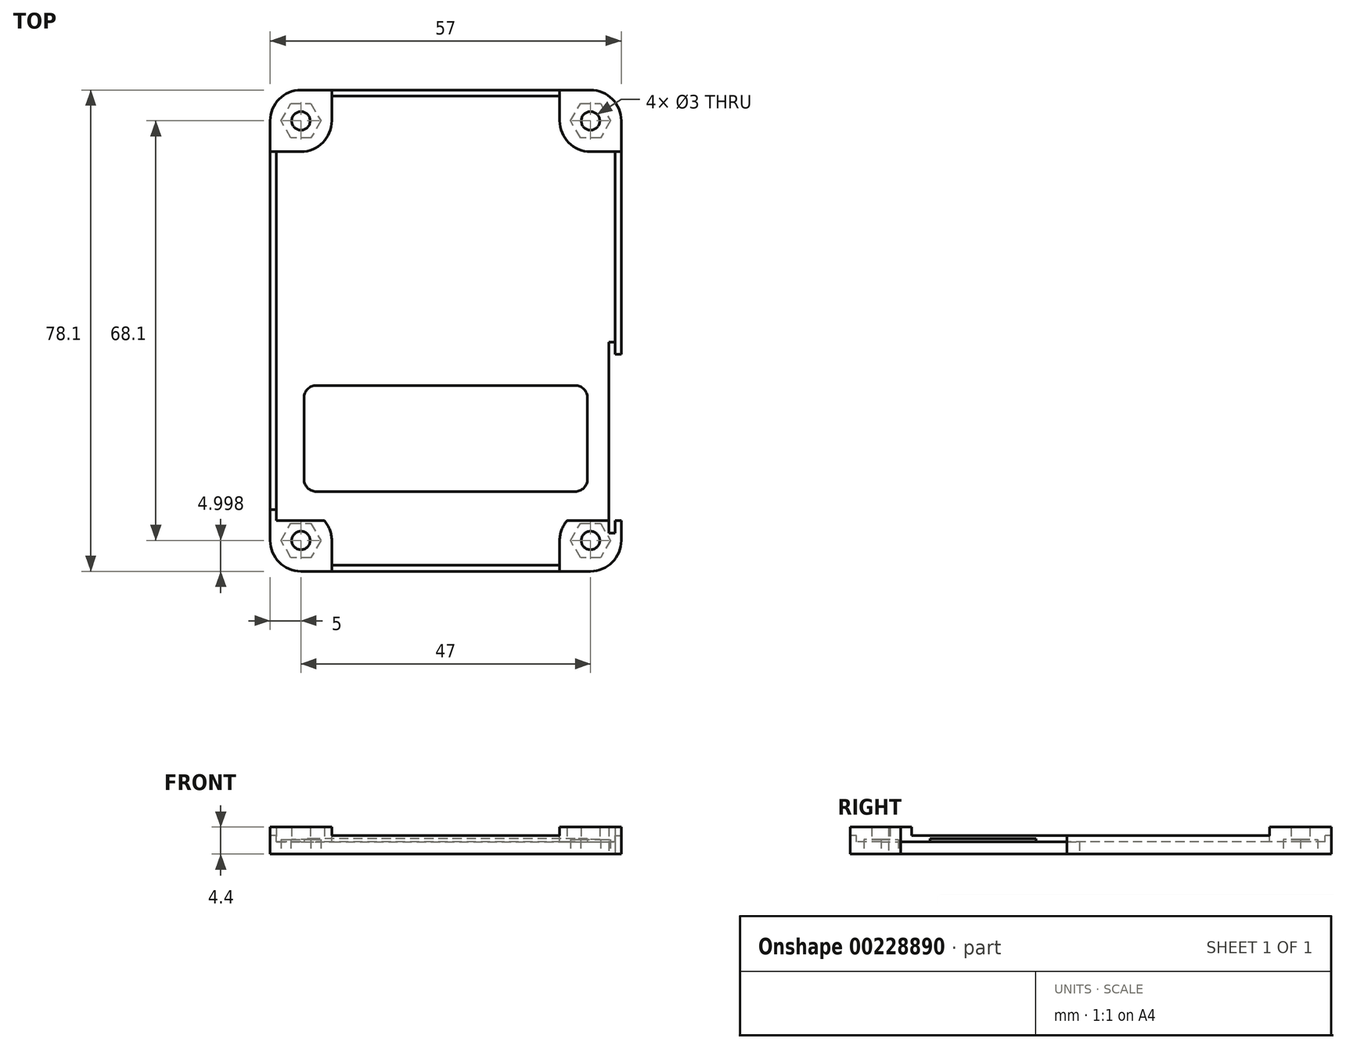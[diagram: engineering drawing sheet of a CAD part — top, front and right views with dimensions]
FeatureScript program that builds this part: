
annotation { "Feature Type Name" : "Feature", "Feature Type Description" : "" }
export const myFeature = defineFeature(function(context is Context, id is Id, definition is map)
    precondition{}
    {
        {
            var Q0;
            Q0=qCreatedBy(makeId("Top.planeOp"),FACE);
            var sketch = newSketch(context, id + "F0", { "sketchPlane" : qUnion([Q0])});
            skLineSegment(sketch, "E0.bottom", {"start": v(-20.39, 18.87) * mm, "end": v(6.91, 18.87) * mm, "construction": true});
            skLineSegment(sketch, "E0.top", {"start": v(-20.39, -8.93) * mm, "end": v(6.91, -8.93) * mm, "construction": true});
            skLineSegment(sketch, "E0.left", {"start": v(-20.39, 18.87) * mm, "end": v(-20.39, -8.93) * mm, "construction": true});
            skLineSegment(sketch, "E0.right", {"start": v(6.91, 18.87) * mm, "end": v(6.91, -8.93) * mm, "construction": true});
            skLineSegment(sketch, "E1.bottom", {"start": v(-24.24, 20.8) * mm, "end": v(10.76, 20.8) * mm, "construction": true});
            skLineSegment(sketch, "E1.top", {"start": v(-24.24, -10.85) * mm, "end": v(10.76, -10.85) * mm, "construction": true});
            skLineSegment(sketch, "E1.left", {"start": v(-24.24, 20.8) * mm, "end": v(-24.24, -10.85) * mm, "construction": true});
            skLineSegment(sketch, "E1.right", {"start": v(10.76, 20.8) * mm, "end": v(10.76, -10.85) * mm, "construction": true});
            skLineSegment(sketch, "E2.bottom", {"start": v(-29.84, -16.15) * mm, "end": v(-29.84, -14.35) * mm, "construction": true});
            skLineSegment(sketch, "E2.top", {"start": v(3.26, -16.15) * mm, "end": v(3.26, -14.35) * mm, "construction": true});
            skLineSegment(sketch, "E2.left", {"start": v(-29.84, -16.15) * mm, "end": v(3.26, -16.15) * mm, "construction": true});
            skLineSegment(sketch, "E2.right", {"start": v(-25.74, -14.35) * mm, "end": v(3.26, -14.35) * mm, "construction": true});
            skLineSegment(sketch, "E3.bottom", {"start": v(-30.74, -14.35) * mm, "end": v(-30.74, -11.95) * mm, "construction": true});
            skLineSegment(sketch, "E3.top", {"start": v(-25.74, -14.35) * mm, "end": v(-25.74, -11.95) * mm, "construction": true});
            skLineSegment(sketch, "E3.left", {"start": v(-30.74, -14.35) * mm, "end": v(-29.84, -14.35) * mm, "construction": true});
            skLineSegment(sketch, "E3.right", {"start": v(-30.74, -11.95) * mm, "end": v(-25.74, -11.95) * mm, "construction": true});
            skLineSegment(sketch, "E4.bottom", {"start": v(-29.34, -20.15) * mm, "end": v(22.16, -20.15) * mm, "construction": true});
            skLineSegment(sketch, "E4.top", {"start": v(-29.34, -46.15) * mm, "end": v(22.16, -46.15) * mm, "construction": true});
            skLineSegment(sketch, "E4.left", {"start": v(-29.34, -20.15) * mm, "end": v(-29.34, -46.15) * mm, "construction": true});
            skLineSegment(sketch, "E4.right", {"start": v(22.16, -20.15) * mm, "end": v(22.16, -46.15) * mm, "construction": true});
            skLineSegment(sketch, "E5.bottom", {"start": v(-26.84, 23.3) * mm, "end": v(20.16, 23.3) * mm});
            skLineSegment(sketch, "E5.top", {"start": v(-26.84, -54.8) * mm, "end": v(20.16, -54.8) * mm});
            skLineSegment(sketch, "E5.left", {"start": v(-31.84, 18.3) * mm, "end": v(-31.84, -49.8) * mm});
            skLineSegment(sketch, "E5.right", {"start": v(25.16, 18.3) * mm, "end": v(25.16, -49.8) * mm});
            skArc(sketch, "E6.filletArc", {"start": v(-26.84, 23.3) * mm, "mid": v(-30.38, 21.83) * mm, "end": v(-31.84, 18.3) * mm});
            skArc(sketch, "E7.filletArc", {"start": v(20.16, -54.8) * mm, "mid": v(23.7, -53.34) * mm, "end": v(25.16, -49.8) * mm});
            skArc(sketch, "E8.filletArc", {"start": v(-31.84, -49.8) * mm, "mid": v(-30.38, -53.34) * mm, "end": v(-26.84, -54.8) * mm});
            skArc(sketch, "E9.filletArc", {"start": v(25.16, 18.3) * mm, "mid": v(23.7, 21.83) * mm, "end": v(20.16, 23.3) * mm});
            skCircle(sketch, "E10", {"center": v(-26.84, 18.3) * mm, "radius": 2.8 * mm, "construction": true});
            skCircle(sketch, "E11", {"center": v(20.16, 18.3) * mm, "radius": 2.8 * mm, "construction": true});
            skCircle(sketch, "E12", {"center": v(20.16, -49.8) * mm, "radius": 2.8 * mm, "construction": true});
            skCircle(sketch, "E13", {"center": v(-26.84, -49.8) * mm, "radius": 2.8 * mm, "construction": true});
            skLineSegment(sketch, "E14", {"start": v(17.96, 15.08) * mm, "end": v(17.96, -13) * mm, "construction": true});
            skLineSegment(sketch, "E15.0", {"start": v(18.54, 21.1) * mm, "end": v(21.78, 21.1) * mm});
            skLineSegment(sketch, "E15.1", {"start": v(21.78, 21.1) * mm, "end": v(23.4, 18.3) * mm});
            skLineSegment(sketch, "E15.2", {"start": v(23.4, 18.3) * mm, "end": v(21.78, 15.5) * mm});
            skLineSegment(sketch, "E15.3", {"start": v(21.78, 15.5) * mm, "end": v(18.54, 15.5) * mm});
            skLineSegment(sketch, "E15.4", {"start": v(18.54, 15.5) * mm, "end": v(16.93, 18.3) * mm});
            skLineSegment(sketch, "E15.5", {"start": v(16.93, 18.3) * mm, "end": v(18.54, 21.1) * mm});
            skPoint(sketch, "E15.0.midPoint", {"position": v(20.16, 21.1) * mm});
            skLineSegment(sketch, "E16.0", {"start": v(-28.46, 21.1) * mm, "end": v(-25.22, 21.1) * mm});
            skLineSegment(sketch, "E16.1", {"start": v(-25.22, 21.1) * mm, "end": v(-23.6, 18.3) * mm});
            skLineSegment(sketch, "E16.2", {"start": v(-23.6, 18.3) * mm, "end": v(-25.22, 15.5) * mm});
            skLineSegment(sketch, "E16.3", {"start": v(-25.22, 15.5) * mm, "end": v(-28.46, 15.5) * mm});
            skLineSegment(sketch, "E16.4", {"start": v(-28.46, 15.5) * mm, "end": v(-30.07, 18.3) * mm});
            skLineSegment(sketch, "E16.5", {"start": v(-30.07, 18.3) * mm, "end": v(-28.46, 21.1) * mm});
            skPoint(sketch, "E16.0.midPoint", {"position": v(-26.84, 21.1) * mm});
            skLineSegment(sketch, "E17.0", {"start": v(18.54, -47) * mm, "end": v(21.78, -47) * mm});
            skLineSegment(sketch, "E17.1", {"start": v(21.78, -47) * mm, "end": v(23.4, -49.8) * mm});
            skLineSegment(sketch, "E17.2", {"start": v(23.4, -49.8) * mm, "end": v(21.78, -52.6) * mm});
            skLineSegment(sketch, "E17.3", {"start": v(21.78, -52.6) * mm, "end": v(18.54, -52.6) * mm});
            skLineSegment(sketch, "E17.4", {"start": v(18.54, -52.6) * mm, "end": v(16.93, -49.8) * mm});
            skLineSegment(sketch, "E17.5", {"start": v(16.93, -49.8) * mm, "end": v(18.54, -47) * mm});
            skPoint(sketch, "E17.0.midPoint", {"position": v(20.16, -47) * mm});
            skLineSegment(sketch, "E18.0", {"start": v(-28.46, -47) * mm, "end": v(-25.22, -47) * mm});
            skLineSegment(sketch, "E18.1", {"start": v(-25.22, -47) * mm, "end": v(-23.6, -49.8) * mm});
            skLineSegment(sketch, "E18.2", {"start": v(-23.6, -49.8) * mm, "end": v(-25.22, -52.6) * mm});
            skLineSegment(sketch, "E18.3", {"start": v(-25.22, -52.6) * mm, "end": v(-28.46, -52.6) * mm});
            skLineSegment(sketch, "E18.4", {"start": v(-28.46, -52.6) * mm, "end": v(-30.07, -49.8) * mm});
            skLineSegment(sketch, "E18.5", {"start": v(-30.07, -49.8) * mm, "end": v(-28.46, -47) * mm});
            skPoint(sketch, "E18.0.midPoint", {"position": v(-26.84, -47) * mm});
            skSolve(sketch);
        }
        {
            var Q0;
            Q0 = qSketchRegion(id + "F0", true);
            extrude(context, id + "F1", {"entities" : qUnion([Q0]), "depth" : 2.4 * mm, "offsetDistance" : 25 * mm});
        }
        {
            var Q0;
            Q0=makeQuery(id+"F1.opExtrude","CAP_FACE",FACE,{"disambiguationData":[OSD([sQuery(id+"F0.wireOp",EDGE,"E5.bottom"),sQuery(id+"F0.wireOp",EDGE,"E5.top"),sQuery(id+"F0.wireOp",EDGE,"E5.left"),sQuery(id+"F0.wireOp",EDGE,"E5.right"),sQuery(id+"F0.wireOp",EDGE,"E6.filletArc"),sQuery(id+"F0.wireOp",EDGE,"E7.filletArc"),sQuery(id+"F0.wireOp",EDGE,"E8.filletArc"),sQuery(id+"F0.wireOp",EDGE,"E9.filletArc"),sQuery(id+"F0.wireOp",EDGE,"E15.0"),sQuery(id+"F0.wireOp",EDGE,"E15.1"),sQuery(id+"F0.wireOp",EDGE,"E15.2"),sQuery(id+"F0.wireOp",EDGE,"E15.3"),sQuery(id+"F0.wireOp",EDGE,"E15.4"),sQuery(id+"F0.wireOp",EDGE,"E15.5"),sQuery(id+"F0.wireOp",EDGE,"E16.0"),sQuery(id+"F0.wireOp",EDGE,"E16.1"),sQuery(id+"F0.wireOp",EDGE,"E16.2"),sQuery(id+"F0.wireOp",EDGE,"E16.3"),sQuery(id+"F0.wireOp",EDGE,"E16.4"),sQuery(id+"F0.wireOp",EDGE,"E16.5"),sQuery(id+"F0.wireOp",EDGE,"E17.0"),sQuery(id+"F0.wireOp",EDGE,"E17.1"),sQuery(id+"F0.wireOp",EDGE,"E17.2"),sQuery(id+"F0.wireOp",EDGE,"E17.3"),sQuery(id+"F0.wireOp",EDGE,"E17.4"),sQuery(id+"F0.wireOp",EDGE,"E17.5"),sQuery(id+"F0.wireOp",EDGE,"E18.0"),sQuery(id+"F0.wireOp",EDGE,"E18.1"),sQuery(id+"F0.wireOp",EDGE,"E18.2"),sQuery(id+"F0.wireOp",EDGE,"E18.3"),sQuery(id+"F0.wireOp",EDGE,"E18.4"),sQuery(id+"F0.wireOp",EDGE,"E18.5")])],"isStart":false});
            var sketch = newSketch(context, id + "F2", { "sketchPlane" : qUnion([Q0])});
            skArc(sketch, "E19", {"start": v(-26.84, 23.3) * mm, "mid": v(-30.38, 21.83) * mm, "end": v(-31.84, 18.3) * mm});
            skArc(sketch, "E20", {"start": v(25.16, 18.3) * mm, "mid": v(23.7, 21.83) * mm, "end": v(20.16, 23.3) * mm});
            skArc(sketch, "E21", {"start": v(16.33, -46.6) * mm, "mid": v(15.46, -48.1) * mm, "end": v(15.16, -49.8) * mm});
            skArc(sketch, "E22", {"start": v(-21.84, -49.8) * mm, "mid": v(-22.14, -48.1) * mm, "end": v(-23, -46.6) * mm});
            skCircle(sketch, "E23", {"center": v(-26.84, 18.3) * mm, "radius": 1.5 * mm});
            skCircle(sketch, "E24", {"center": v(20.16, 18.3) * mm, "radius": 1.5 * mm});
            skCircle(sketch, "E25", {"center": v(20.16, -49.8) * mm, "radius": 1.5 * mm});
            skCircle(sketch, "E26", {"center": v(-26.84, -49.8) * mm, "radius": 1.5 * mm});
            skLineSegment(sketch, "E27.bottom", {"start": v(-21.84, 23.3) * mm, "end": v(-26.84, 23.3) * mm});
            skLineSegment(sketch, "E27.top", {"start": v(-26.84, 13.3) * mm, "end": v(-31.84, 13.3) * mm});
            skLineSegment(sketch, "E27.left", {"start": v(-21.84, 23.3) * mm, "end": v(-21.84, 18.3) * mm});
            skLineSegment(sketch, "E27.right", {"start": v(-31.84, 18.3) * mm, "end": v(-31.84, 13.3) * mm});
            skLineSegment(sketch, "E28.bottom", {"start": v(15.16, 23.3) * mm, "end": v(20.16, 23.3) * mm});
            skLineSegment(sketch, "E28.top", {"start": v(20.16, 13.3) * mm, "end": v(25.16, 13.3) * mm});
            skLineSegment(sketch, "E28.left", {"start": v(15.16, 23.3) * mm, "end": v(15.16, 18.3) * mm});
            skLineSegment(sketch, "E28.right", {"start": v(25.16, 18.3) * mm, "end": v(25.16, 13.3) * mm});
            skLineSegment(sketch, "E29.bottom", {"start": v(25.16, -44.8) * mm, "end": v(24.16, -44.8) * mm});
            skLineSegment(sketch, "E29.top", {"start": v(20.16, -54.8) * mm, "end": v(15.16, -54.8) * mm});
            skLineSegment(sketch, "E29.left", {"start": v(25.16, -44.8) * mm, "end": v(25.16, -49.8) * mm});
            skLineSegment(sketch, "E29.right", {"start": v(15.16, -49.8) * mm, "end": v(15.16, -54.8) * mm});
            skLineSegment(sketch, "E30.bottom", {"start": v(-31.84, -44.8) * mm, "end": v(-30.84, -44.8) * mm});
            skLineSegment(sketch, "E30.top", {"start": v(-26.84, -54.8) * mm, "end": v(-21.84, -54.8) * mm});
            skLineSegment(sketch, "E30.left", {"start": v(-31.84, -44.8) * mm, "end": v(-31.84, -49.8) * mm});
            skLineSegment(sketch, "E30.right", {"start": v(-21.84, -49.8) * mm, "end": v(-21.84, -54.8) * mm});
            skArc(sketch, "E31.trimOffspring", {"start": v(-26.84, 13.3) * mm, "mid": v(-23.3, 14.76) * mm, "end": v(-21.84, 18.3) * mm});
            skArc(sketch, "E32.trimOffspring", {"start": v(15.16, 18.3) * mm, "mid": v(16.62, 14.76) * mm, "end": v(20.16, 13.3) * mm});
            skArc(sketch, "E33.trimOffspring", {"start": v(20.16, -54.8) * mm, "mid": v(23.7, -53.34) * mm, "end": v(25.16, -49.8) * mm});
            skArc(sketch, "E34.trimOffspring", {"start": v(-31.84, -49.8) * mm, "mid": v(-30.38, -53.34) * mm, "end": v(-26.84, -54.8) * mm});
            skLineSegment(sketch, "E35.bottom", {"start": v(-21.84, 23.3) * mm, "end": v(15.16, 23.3) * mm});
            skLineSegment(sketch, "E35.top", {"start": v(-21.84, 22.3) * mm, "end": v(15.16, 22.3) * mm});
            skLineSegment(sketch, "E35.left", {"start": v(-21.84, 23.3) * mm, "end": v(-21.84, 22.3) * mm});
            skLineSegment(sketch, "E35.right", {"start": v(15.16, 23.3) * mm, "end": v(15.16, 22.3) * mm});
            skLineSegment(sketch, "E36.bottom", {"start": v(-21.84, -54.8) * mm, "end": v(15.16, -54.8) * mm});
            skLineSegment(sketch, "E36.top", {"start": v(-21.84, -53.8) * mm, "end": v(15.16, -53.8) * mm});
            skLineSegment(sketch, "E36.left", {"start": v(-21.84, -54.8) * mm, "end": v(-21.84, -53.8) * mm});
            skLineSegment(sketch, "E36.right", {"start": v(15.16, -54.8) * mm, "end": v(15.16, -53.8) * mm});
            skLineSegment(sketch, "E37.bottom", {"start": v(25.16, 13.3) * mm, "end": v(24.16, 13.3) * mm});
            skLineSegment(sketch, "E37.left", {"start": v(25.16, 13.3) * mm, "end": v(25.16, -44.8) * mm});
            skLineSegment(sketch, "E37.right", {"start": v(24.16, 13.3) * mm, "end": v(24.16, -44.8) * mm});
            skLineSegment(sketch, "E38.bottom", {"start": v(-31.84, 13.3) * mm, "end": v(-30.84, 13.3) * mm});
            skLineSegment(sketch, "E38.left", {"start": v(-31.84, 13.3) * mm, "end": v(-31.84, -44.8) * mm});
            skLineSegment(sketch, "E38.right", {"start": v(-30.84, 13.3) * mm, "end": v(-30.84, -44.8) * mm});
            skLineSegment(sketch, "E39.top", {"start": v(-30.84, -46.6) * mm, "end": v(-23, -46.6) * mm});
            skLineSegment(sketch, "E39.left", {"start": v(-30.84, -43.24) * mm, "end": v(-30.84, -46.6) * mm});
            skLineSegment(sketch, "E39.right", {"start": v(24.16, -43.24) * mm, "end": v(24.16, -46.6) * mm});
            skLineSegment(sketch, "E40.trimOffspring", {"start": v(16.33, -46.6) * mm, "end": v(24.16, -46.6) * mm});
            skSolve(sketch);
        }
        {
            var Q0;
            Q0=makeQuery(id+"F2.imprint","IMPRINT",FACE,{"disambiguationData":[TD([[makeQuery(id+"F2.imprint","IMPRINT",EDGE,{"derivedFrom":sQuery(id+"F2.wireOp",EDGE,"E19")}),1.0]])]});
            var Q1;
            Q1=makeQuery(id+"F2.imprint","IMPRINT",FACE,{"disambiguationData":[TD([[makeQuery(id+"F2.imprint","IMPRINT",EDGE,{"derivedFrom":sQuery(id+"F2.wireOp",EDGE,"E20")}),1.0]])]});
            var Q2;
            {var subQ3=sQuery(id+"F2.wireOp",EDGE,"E21");Q2=makeQuery(id+"F2.imprint","IMPRINT",FACE,{"disambiguationData":[TD([[makeQuery(id+"F2.imprint","IMPRINT",EDGE,{"derivedFrom":subQ3}),1.0]])]});}
            var Q3;
            {var subQ3=sQuery(id+"F2.wireOp",EDGE,"E22");Q3=makeQuery(id+"F2.imprint","IMPRINT",FACE,{"disambiguationData":[TD([[makeQuery(id+"F2.imprint","IMPRINT",EDGE,{"derivedFrom":subQ3}),1.0]])]});}
            var Q4;
            Q4=makeQuery(id+"F2.imprint","IMPRINT",FACE,{"disambiguationData":[TD([[makeQuery(id+"F2.imprint","IMPRINT",EDGE,{"derivedFrom":sQuery(id+"F2.wireOp",EDGE,"E26")}),-1.0]])]});
            var Q5;
            Q5=makeQuery(id+"F2.imprint","IMPRINT",FACE,{"disambiguationData":[TD([[makeQuery(id+"F2.imprint","IMPRINT",EDGE,{"derivedFrom":sQuery(id+"F2.wireOp",EDGE,"E25")}),-1.0]])]});
            var Q6;
            Q6=makeQuery(id+"F2.imprint","IMPRINT",FACE,{"disambiguationData":[TD([[makeQuery(id+"F2.imprint","IMPRINT",EDGE,{"derivedFrom":sQuery(id+"F2.wireOp",EDGE,"E24")}),-1.0]])]});
            var Q7;
            Q7=makeQuery(id+"F2.imprint","IMPRINT",FACE,{"disambiguationData":[TD([[makeQuery(id+"F2.imprint","IMPRINT",EDGE,{"derivedFrom":sQuery(id+"F2.wireOp",EDGE,"E23")}),-1.0]])]});
            extrude(context, id + "F3", {"entities" : qUnion([Q0, Q1, Q2, Q3, Q4, Q5, Q6, Q7]), "operationType" : NewBodyOperationType.ADD, "depth" : 2 * mm, "offsetDistance" : 25 * mm});
        }
        {
            var Q0;
            {var subQ2=sQuery(id+"F2.wireOp",EDGE,"E21");Q0=makeQuery(id+"F2.imprint","IMPRINT",FACE,{"disambiguationData":[TD([[makeQuery(id+"F2.imprint","IMPRINT",EDGE,{"derivedFrom":subQ2}),-1.0]])]});}
            extrude(context, id + "F4", {"entities" : qUnion([Q0]), "operationType" : NewBodyOperationType.REMOVE, "oppositeDirection" : true, "depth" : 0.4 * mm, "offsetDistance" : 25 * mm});
        }
        {
            var Q0;
            {var subQ5=sQuery(id+"F2.wireOp",EDGE,"E30.bottom");Q0=makeQuery(id+"F2.imprint","IMPRINT",FACE,{"disambiguationData":[TD([[makeQuery(id+"F2.imprint","IMPRINT",EDGE,{"derivedFrom":subQ5}),1.0]])]});}
            var Q1;
            {var subQ0=sQuery(id+"F2.wireOp",EDGE,"E35.bottom");Q1=makeQuery(id+"F2.imprint","IMPRINT",FACE,{"disambiguationData":[TD([[makeQuery(id+"F2.imprint","IMPRINT",EDGE,{"derivedFrom":subQ0}),-1.0]])]});}
            var Q2;
            {var subQ5=sQuery(id+"F2.wireOp",EDGE,"E29.bottom");Q2=makeQuery(id+"F2.imprint","IMPRINT",FACE,{"disambiguationData":[TD([[makeQuery(id+"F2.imprint","IMPRINT",EDGE,{"derivedFrom":subQ5}),-1.0]])]});}
            var Q3;
            {var subQ0=sQuery(id+"F2.wireOp",EDGE,"E36.bottom");Q3=makeQuery(id+"F2.imprint","IMPRINT",FACE,{"disambiguationData":[TD([[makeQuery(id+"F2.imprint","IMPRINT",EDGE,{"derivedFrom":subQ0}),1.0]])]});}
            extrude(context, id + "F5", {"entities" : qUnion([Q0, Q1, Q2, Q3]), "operationType" : NewBodyOperationType.ADD, "depth" : 0.6 * mm, "offsetDistance" : 25 * mm});
        }
        {
            var Q0;
            Q0=makeQuery(id+"F1.opExtrude","CAP_FACE",FACE,{"disambiguationData":[OSD([sQuery(id+"F0.wireOp",EDGE,"E5.bottom"),sQuery(id+"F0.wireOp",EDGE,"E5.top"),sQuery(id+"F0.wireOp",EDGE,"E5.left"),sQuery(id+"F0.wireOp",EDGE,"E5.right"),sQuery(id+"F0.wireOp",EDGE,"E6.filletArc"),sQuery(id+"F0.wireOp",EDGE,"E7.filletArc"),sQuery(id+"F0.wireOp",EDGE,"E8.filletArc"),sQuery(id+"F0.wireOp",EDGE,"E9.filletArc"),sQuery(id+"F0.wireOp",EDGE,"E15.0"),sQuery(id+"F0.wireOp",EDGE,"E15.1"),sQuery(id+"F0.wireOp",EDGE,"E15.2"),sQuery(id+"F0.wireOp",EDGE,"E15.3"),sQuery(id+"F0.wireOp",EDGE,"E15.4"),sQuery(id+"F0.wireOp",EDGE,"E15.5"),sQuery(id+"F0.wireOp",EDGE,"E16.0"),sQuery(id+"F0.wireOp",EDGE,"E16.1"),sQuery(id+"F0.wireOp",EDGE,"E16.2"),sQuery(id+"F0.wireOp",EDGE,"E16.3"),sQuery(id+"F0.wireOp",EDGE,"E16.4"),sQuery(id+"F0.wireOp",EDGE,"E16.5"),sQuery(id+"F0.wireOp",EDGE,"E17.0"),sQuery(id+"F0.wireOp",EDGE,"E17.1"),sQuery(id+"F0.wireOp",EDGE,"E17.2"),sQuery(id+"F0.wireOp",EDGE,"E17.3"),sQuery(id+"F0.wireOp",EDGE,"E17.4"),sQuery(id+"F0.wireOp",EDGE,"E17.5"),sQuery(id+"F0.wireOp",EDGE,"E18.0"),sQuery(id+"F0.wireOp",EDGE,"E18.1"),sQuery(id+"F0.wireOp",EDGE,"E18.2"),sQuery(id+"F0.wireOp",EDGE,"E18.3"),sQuery(id+"F0.wireOp",EDGE,"E18.4"),sQuery(id+"F0.wireOp",EDGE,"E18.5")])],"isStart":true});
            var sketch = newSketch(context, id + "F6", { "sketchPlane" : qUnion([Q0])});
            skLineSegment(sketch, "E41.bottom", {"start": v(25.16, 19.6) * mm, "end": v(24.16, 19.6) * mm});
            skLineSegment(sketch, "E41.top", {"start": v(25.16, 46.6) * mm, "end": v(24.16, 46.6) * mm});
            skLineSegment(sketch, "E41.left", {"start": v(25.16, 19.6) * mm, "end": v(25.16, 46.6) * mm});
            skLineSegment(sketch, "E41.right", {"start": v(23.16, 19.6) * mm, "end": v(23.16, 46.6) * mm});
            skLineSegment(sketch, "E42.top", {"start": v(23.16, 17.6) * mm, "end": v(24.16, 17.6) * mm});
            skLineSegment(sketch, "E42.left", {"start": v(23.16, 19.6) * mm, "end": v(23.16, 17.6) * mm});
            skLineSegment(sketch, "E42.right", {"start": v(24.16, 19.6) * mm, "end": v(24.16, 17.6) * mm});
            skLineSegment(sketch, "E43.top", {"start": v(23.16, 48.6) * mm, "end": v(24.16, 48.6) * mm});
            skLineSegment(sketch, "E43.left", {"start": v(23.16, 46.6) * mm, "end": v(23.16, 48.6) * mm});
            skLineSegment(sketch, "E43.right", {"start": v(24.16, 46.6) * mm, "end": v(24.16, 48.6) * mm});
            skSolve(sketch);
        }
        {
            var Q0;
            Q0=makeQuery(id+"F6.imprint","IMPRINT",FACE,{"disambiguationData":[TD([[makeQuery(id+"F6.imprint","IMPRINT",EDGE,{"derivedFrom":sQuery(id+"F6.wireOp",EDGE,"E41.bottom")}),-1.0]])]});
            extrude(context, id + "F7", {"entities" : qUnion([Q0]), "operationType" : NewBodyOperationType.REMOVE, "oppositeDirection" : true, "depth" : 4.4 * mm, "offsetDistance" : 25 * mm});
        }
        {
            var Q0;
            Q0=makeQuery(id+"F4.boolean.opBoolean","COPY",FACE,{"derivedFrom":makeQuery(id+"F4.opExtrude","CAP_FACE",FACE,{"disambiguationData":[OSD([sQuery(id+"F2.wireOp",EDGE,"E21"),sQuery(id+"F2.wireOp",EDGE,"E22"),sQuery(id+"F2.wireOp",EDGE,"E27.top"),sQuery(id+"F2.wireOp",EDGE,"E27.left"),sQuery(id+"F2.wireOp",EDGE,"E28.top"),sQuery(id+"F2.wireOp",EDGE,"E28.left"),sQuery(id+"F2.wireOp",EDGE,"E29.right"),sQuery(id+"F2.wireOp",EDGE,"E30.right"),sQuery(id+"F2.wireOp",EDGE,"E31.trimOffspring"),sQuery(id+"F2.wireOp",EDGE,"E32.trimOffspring"),sQuery(id+"F2.wireOp",EDGE,"E35.top"),sQuery(id+"F2.wireOp",EDGE,"E36.top"),sQuery(id+"F2.wireOp",EDGE,"E37.right"),sQuery(id+"F2.wireOp",EDGE,"E38.right"),sQuery(id+"F2.wireOp",EDGE,"E39.top"),sQuery(id+"F2.wireOp",EDGE,"E39.left"),sQuery(id+"F2.wireOp",EDGE,"E39.right"),sQuery(id+"F2.wireOp",EDGE,"E40.trimOffspring")])],"isStart":false})});
            var sketch = newSketch(context, id + "F8", { "sketchPlane" : qUnion([Q0])});
            skLineSegment(sketch, "E44.bottom", {"start": v(17.66, -24.64) * mm, "end": v(-24.34, -24.64) * mm});
            skLineSegment(sketch, "E44.top", {"start": v(17.66, -41.87) * mm, "end": v(-24.34, -41.87) * mm});
            skLineSegment(sketch, "E44.left", {"start": v(19.66, -26.64) * mm, "end": v(19.66, -39.87) * mm});
            skLineSegment(sketch, "E44.right", {"start": v(-26.34, -26.64) * mm, "end": v(-26.34, -39.87) * mm});
            skPoint(sketch, "E45.visualSharp", {"position": v(-26.34, -24.64) * mm});
            skArc(sketch, "E45.filletArc", {"start": v(-24.34, -24.64) * mm, "mid": v(-25.76, -25.23) * mm, "end": v(-26.34, -26.64) * mm});
            skPoint(sketch, "E46.visualSharp", {"position": v(19.66, -24.64) * mm});
            skArc(sketch, "E46.filletArc", {"start": v(19.66, -26.64) * mm, "mid": v(19.08, -25.23) * mm, "end": v(17.66, -24.64) * mm});
            skPoint(sketch, "E47.visualSharp", {"position": v(19.66, -41.87) * mm});
            skArc(sketch, "E47.filletArc", {"start": v(17.66, -41.87) * mm, "mid": v(19.08, -41.28) * mm, "end": v(19.66, -39.87) * mm});
            skPoint(sketch, "E48.visualSharp", {"position": v(-26.34, -41.87) * mm});
            skArc(sketch, "E48.filletArc", {"start": v(-26.34, -39.87) * mm, "mid": v(-25.76, -41.28) * mm, "end": v(-24.34, -41.87) * mm});
            skSolve(sketch);
        }
        {
            var Q0;
            Q0 = qSketchRegion(id + "F8", true);
            extrude(context, id + "F9", {"entities" : qUnion([Q0]), "operationType" : NewBodyOperationType.ADD, "depth" : 0.5 * mm, "offsetDistance" : 25 * mm});
        }
    });
